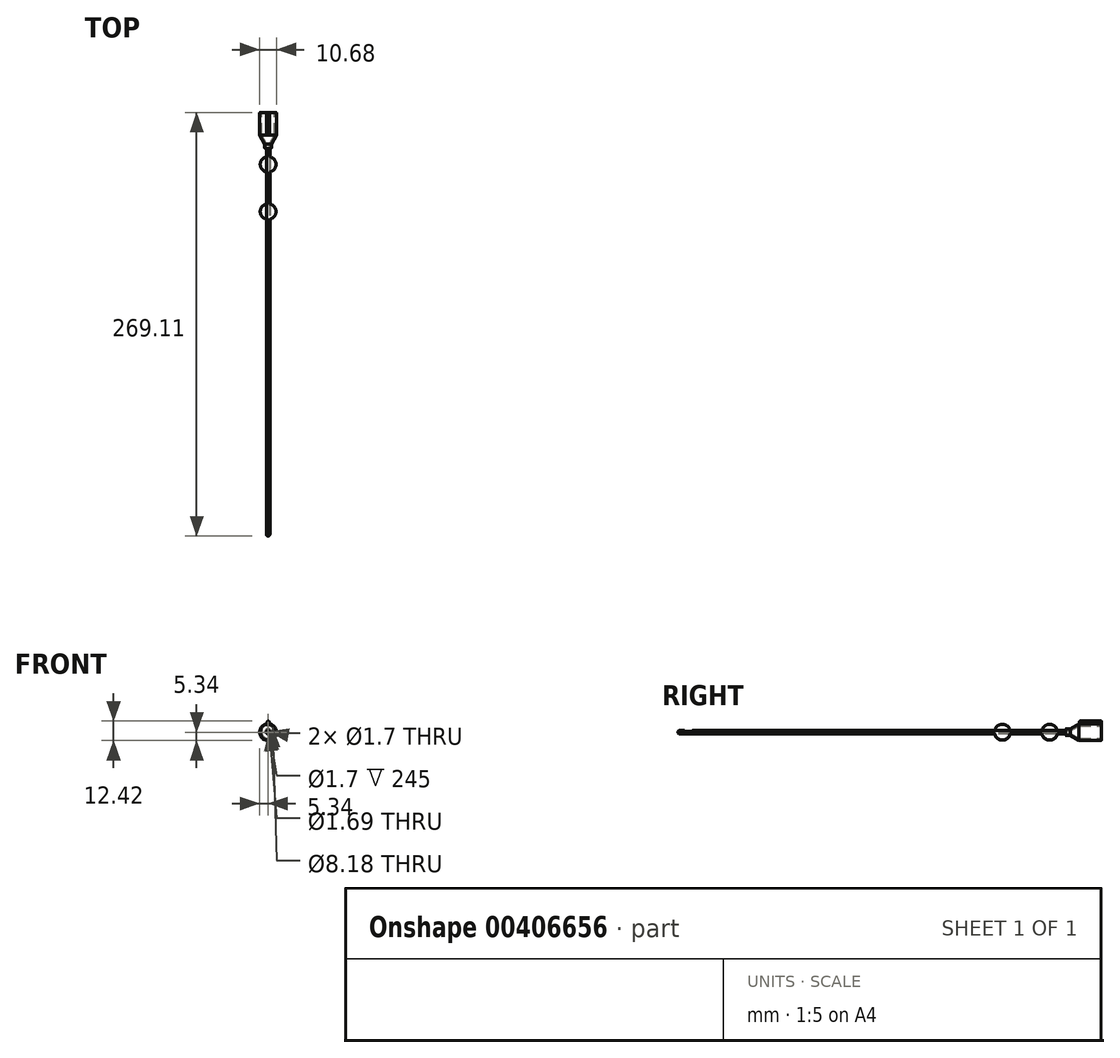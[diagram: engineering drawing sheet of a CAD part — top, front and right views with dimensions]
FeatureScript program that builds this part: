
annotation { "Feature Type Name" : "Feature", "Feature Type Description" : "" }
export const myFeature = defineFeature(function(context is Context, id is Id, definition is map)
    precondition{}
    {
        {
            var Q0;
            Q0=qCreatedBy(makeId("Front.planeOp"),FACE);
            var sketch = newSketch(context, id + "F0", { "sketchPlane" : qUnion([Q0])});
            skCircle(sketch, "E0", {"center": v(0, 0) * mm, "radius": 0.85 * mm});
            skCircle(sketch, "E1.0", {"center": v(0, 0) * mm, "radius": 1.1 * mm});
            skSolve(sketch);
        }
        {
            var Q0;
            Q0=qCreatedBy(makeId("Top.planeOp"),FACE);
            var sketch = newSketch(context, id + "F1", { "sketchPlane" : qUnion([Q0])});
            skLineSegment(sketch, "E2.bottom", {"start": v(-0.9, 8) * mm, "end": v(0.9, 8) * mm});
            skLineSegment(sketch, "E2.top", {"start": v(-0.9, 3) * mm, "end": v(0.9, 3) * mm});
            skLineSegment(sketch, "E2.left", {"start": v(-0.9, 8) * mm, "end": v(-0.9, 3) * mm});
            skLineSegment(sketch, "E2.right", {"start": v(0.9, 8) * mm, "end": v(0.9, 3) * mm});
            skPoint(sketch, "E2.middle", {"position": v(0, 5.5) * mm});
            skArc(sketch, "E3", {"start": v(-0.85, 0) * mm, "mid": v(-0.6, -0.58) * mm, "end": v(0, -0.82) * mm});
            skArc(sketch, "E4.0", {"start": v(-1.1, 0) * mm, "mid": v(-0.77, -0.76) * mm, "end": v(0, -1.08) * mm});
            skLineSegment(sketch, "E5", {"start": v(-1.1, 0) * mm, "end": v(-0.85, 0) * mm});
            skLineSegment(sketch, "E6", {"start": v(0.85, 0) * mm, "end": v(1.1, 0) * mm});
            skLineSegment(sketch, "E7", {"start": v(-0.85, 0) * mm, "end": v(-1.1, 0) * mm});
            skLineSegment(sketch, "E8", {"start": v(0, 247.63) * mm, "end": v(0, -1.55) * mm});
            skPoint(sketch, "E8.endSnap0", {"position": v(0, -0.82) * mm});
            skSolve(sketch);
        }
        {
            var Q0;
            Q0=makeQuery(id+"F0.imprint","IMPRINT",FACE,{"disambiguationData":[TD([[makeQuery(id+"F0.imprint","IMPRINT",EDGE,{"derivedFrom":sQuery(id+"F0.wireOp",EDGE,"E0")}),-1.0]])]});
            extrude(context, id + "F2", {"entities" : qUnion([Q0]), "oppositeDirection" : true, "depth" : 245 * mm});
        }
        {
            var Q0;
            {var subQ0=sQuery(id+"F1.wireOp",EDGE,"E2.left");Q0=makeQuery(id+"F1.imprint","IMPRINT",FACE,{"disambiguationData":[TD([[makeQuery(id+"F1.imprint","IMPRINT",EDGE,{"derivedFrom":subQ0}),1.0]])]});}
            var Q1;
            {var subQ0=sQuery(id+"F1.wireOp",EDGE,"E2.right");Q1=makeQuery(id+"F1.imprint","IMPRINT",FACE,{"disambiguationData":[TD([[makeQuery(id+"F1.imprint","IMPRINT",EDGE,{"derivedFrom":subQ0}),-1.0]])]});}
            extrude(context, id + "F3", {"entities" : qUnion([Q0, Q1]), "operationType" : NewBodyOperationType.REMOVE, "depth" : 2 * mm});
        }
        {
            var Q0;
            Q0=qCreatedBy(makeId("Right.planeOp"),FACE);
            var sketch = newSketch(context, id + "F4", { "sketchPlane" : qUnion([Q0])});
            skLineSegment(sketch, "E9", {"start": v(245.03, 0.84) * mm, "end": v(245.03, 2.1) * mm});
            skLineSegment(sketch, "E10", {"start": v(245.03, 2.1) * mm, "end": v(248.03, 2.1) * mm});
            skLineSegment(sketch, "E11", {"start": v(248.03, 2.1) * mm, "end": v(253.65, 5.34) * mm});
            skLineSegment(sketch, "E12", {"start": v(253.65, 5.34) * mm, "end": v(268.03, 5.34) * mm});
            skLineSegment(sketch, "E13", {"start": v(245.03, 0.84) * mm, "end": v(248.03, 0.84) * mm});
            skLineSegment(sketch, "E14", {"start": v(248.03, 0.84) * mm, "end": v(253.65, 4.1) * mm});
            skLineSegment(sketch, "E15", {"start": v(253.65, 4.1) * mm, "end": v(268.03, 4.1) * mm});
            skLineSegment(sketch, "E16", {"start": v(268.03, 4.1) * mm, "end": v(268.03, 5.34) * mm});
            skArc(sketch, "E17", {"start": v(240, 0) * mm, "mid": v(235, 5) * mm, "end": v(230, 0) * mm});
            skArc(sketch, "E18", {"start": v(210, 0) * mm, "mid": v(205, 5) * mm, "end": v(200, 0) * mm});
            skLineSegment(sketch, "E19", {"start": v(200, 0) * mm, "end": v(210, 0) * mm});
            skLineSegment(sketch, "E20", {"start": v(230, 0) * mm, "end": v(240, 0) * mm});
            skSolve(sketch);
        }
        {
            var Q0;
            Q0=makeQuery(id+"F4.imprint","IMPRINT",FACE,{"disambiguationData":[TD([[makeQuery(id+"F4.imprint","IMPRINT",EDGE,{"derivedFrom":sQuery(id+"F4.wireOp",EDGE,"E9")}),-1.0]])]});
            var Q1;
            Q1=sQuery(id+"F1.wireOp",EDGE,"E8");
            revolve(context, id + "F5", {"entities" : qUnion([Q0]), "axis" : qUnion([Q1]), "revolveType" : RevolveType.FULL});
        }
        {
            var Q0;
            Q0=makeQuery(id+"F5.opRevolve","SWEPT_FACE",FACE,{"disambiguationData":[OSD([sQuery(id+"F4.wireOp",EDGE,"E16")])]});
            cPlane(context, id + "F6", {"entities" : qUnion([Q0]), "cplaneType" : CPlaneType.OFFSET, "offset" : 0 * mm, "width" : 150 * mm, "height" : 150 * mm});
        }
        {
            var Q0;
            Q0=qCreatedBy(id+"F6.planeOp",FACE);
            var sketch = newSketch(context, id + "F7", { "sketchPlane" : qUnion([Q0])});
            skLineSegment(sketch, "E21", {"start": v(-1, 5.25) * mm, "end": v(0, 8.08) * mm});
            skLineSegment(sketch, "E22", {"start": v(0, 8.08) * mm, "end": v(1, 5.25) * mm});
            skLineSegment(sketch, "E23", {"start": v(-1, 5.25) * mm, "end": v(1, 5.25) * mm});
            skSolve(sketch);
        }
        {
            var Q0;
            Q0 = qSketchRegion(id + "F7", true);
            extrude(context, id + "F8", {"entities" : qUnion([Q0]), "operationType" : NewBodyOperationType.ADD, "oppositeDirection" : true, "depth" : 14 * mm});
        }
        {
            var Q0;
            Q0=makeQuery(id+"F5.opRevolve","SWEPT_EDGE",EDGE,{"disambiguationData":[OSD([sQuery(id+"F4.wireOp",EDGE,"E15"),sQuery(id+"F4.wireOp",EDGE,"E16")])]});
            var Q1;
            Q1=makeQuery(id+"F8.opExtrude","CAP_EDGE",EDGE,{"disambiguationData":[OSD([sQuery(id+"F7.wireOp",EDGE,"E21")])],"isStart":true});
            var Q2;
            Q2=makeQuery(id+"F8.opExtrude","CAP_EDGE",EDGE,{"disambiguationData":[OSD([sQuery(id+"F7.wireOp",EDGE,"E22")])],"isStart":true});
            var Q3;
            Q3=makeQuery(id+"F5.opRevolve","SWEPT_EDGE",EDGE,{"disambiguationData":[OSD([sQuery(id+"F4.wireOp",EDGE,"E12"),sQuery(id+"F4.wireOp",EDGE,"E16")])]});
            var Q4;
            Q4=makeQuery(id+"F5.opRevolve","SWEPT_EDGE",EDGE,{"disambiguationData":[OSD([sQuery(id+"F4.wireOp",EDGE,"E9"),sQuery(id+"F4.wireOp",EDGE,"E10")])]});
            var Q5;
            Q5=makeQuery(id+"F8.opExtrude","CAP_EDGE",EDGE,{"disambiguationData":[OSD([sQuery(id+"F7.wireOp",EDGE,"E21")])],"isStart":false});
            var Q6;
            Q6=makeQuery(id+"F8.opExtrude","CAP_EDGE",EDGE,{"disambiguationData":[OSD([sQuery(id+"F7.wireOp",EDGE,"E22")])],"isStart":false});
            var Q7;
            Q7=makeQuery(id+"F8.opExtrude","SWEPT_EDGE",EDGE,{"disambiguationData":[OSD([sQuery(id+"F7.wireOp",EDGE,"E21"),sQuery(id+"F7.wireOp",EDGE,"E22")])]});
            fillet(context, id + "F9", {"entities" : qUnion([Q0, Q1, Q2, Q3, Q4, Q5, Q6, Q7]), "radius" : 0.5 * mm, "tangentPropagation" : true, "allowEdgeOverflow" : false});
        }
        {
            var Q0;
            Q0=makeQuery(id+"F4.imprint","IMPRINT",FACE,{"disambiguationData":[TD([[makeQuery(id+"F4.imprint","IMPRINT",EDGE,{"derivedFrom":sQuery(id+"F4.wireOp",EDGE,"E18")}),1.0]])]});
            var Q1;
            Q1=sQuery(id+"F1.wireOp",EDGE,"E8");
            revolve(context, id + "F10", {"entities" : qUnion([Q0]), "axis" : qUnion([Q1]), "revolveType" : RevolveType.FULL});
        }
        {
            var Q0;
            Q0=makeQuery(id+"F4.imprint","IMPRINT",FACE,{"disambiguationData":[TD([[makeQuery(id+"F4.imprint","IMPRINT",EDGE,{"derivedFrom":sQuery(id+"F4.wireOp",EDGE,"E17")}),1.0]])]});
            var Q1;
            Q1=sQuery(id+"F1.wireOp",EDGE,"E8");
            revolve(context, id + "F11", {"entities" : qUnion([Q0]), "axis" : qUnion([Q1]), "revolveType" : RevolveType.FULL});
        }
        {
            var Q0;
            {var subQ0=sQuery(id+"F1.wireOp",EDGE,"E3");Q0=makeQuery(id+"F1.imprint","IMPRINT",FACE,{"disambiguationData":[TD([[makeQuery(id+"F1.imprint","IMPRINT",EDGE,{"derivedFrom":subQ0}),-1.0]])]});}
            var Q1;
            Q1=sQuery(id+"F1.wireOp",EDGE,"E8");
            revolve(context, id + "F12", {"operationType" : NewBodyOperationType.ADD, "entities" : qUnion([Q0]), "axis" : qUnion([Q1]), "revolveType" : RevolveType.FULL});
        }
        {
            var Q0;
            Q0=makeQuery(id+"F0.imprint","IMPRINT",FACE,{"disambiguationData":[TD([[makeQuery(id+"F0.imprint","IMPRINT",EDGE,{"derivedFrom":sQuery(id+"F0.wireOp",EDGE,"E0")}),1.0]])]});
            extrude(context, id + "F13", {"entities" : qUnion([Q0]), "operationType" : NewBodyOperationType.REMOVE, "oppositeDirection" : true, "depth" : 245 * mm});
        }
    });
